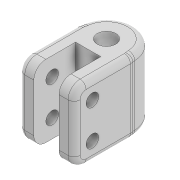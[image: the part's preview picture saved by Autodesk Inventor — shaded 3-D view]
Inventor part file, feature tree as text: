
AUTODESK INVENTOR PART (.ipt)
format: ipt  version: 2022 (Build 260153000, 153)  size: 216,576 bytes
history: native  units: mm
features: extrude x4, sketch x3, fillet x3
ambient origin geometry x8: Origin, YZ Plane, XZ Plane, XY Plane, X Axis, Y Axis, Z Axis, Center Point
bodies: Solid1 (feature_tree)
feature tree (10):
  extrude  "Extrusion1"  Depth=9.0mm
  sketch  "Sketch2"  dims[d2=12.0mm d3=0.0mm d4=4.2mm]
  extrude  "Extrusion2"  Depth=4.2mm
  extrude  "Extrusion4"  Depth=2.5mm
  extrude  "Extrusion3"  Depth=2.5mm
  fillet  "Fillet2"  Radius=10.0mm
  fillet  "Fillet3"  Radius=12.0mm
  fillet  "Fillet4"  Radius=2.1mm
  sketch  "Sketch1"  dims[d0=3.1mm d1=9.0mm]
  sketch  "Sketch3"  dims[d5=2.1mm d6=2.5mm d7=2.5mm d8=10.0mm d9=12.0mm d10=0.0mm d11=2.1mm d12=2.1mm d13=2.0mm d14=2.0mm d17=11.0mm d18=0.0mm d20=2.0mm d21=2.0mm d22=1.0mm d23=20.0mm d24=0.0mm d25=1.5mm d26=5.9mm d27=3.05mm]
